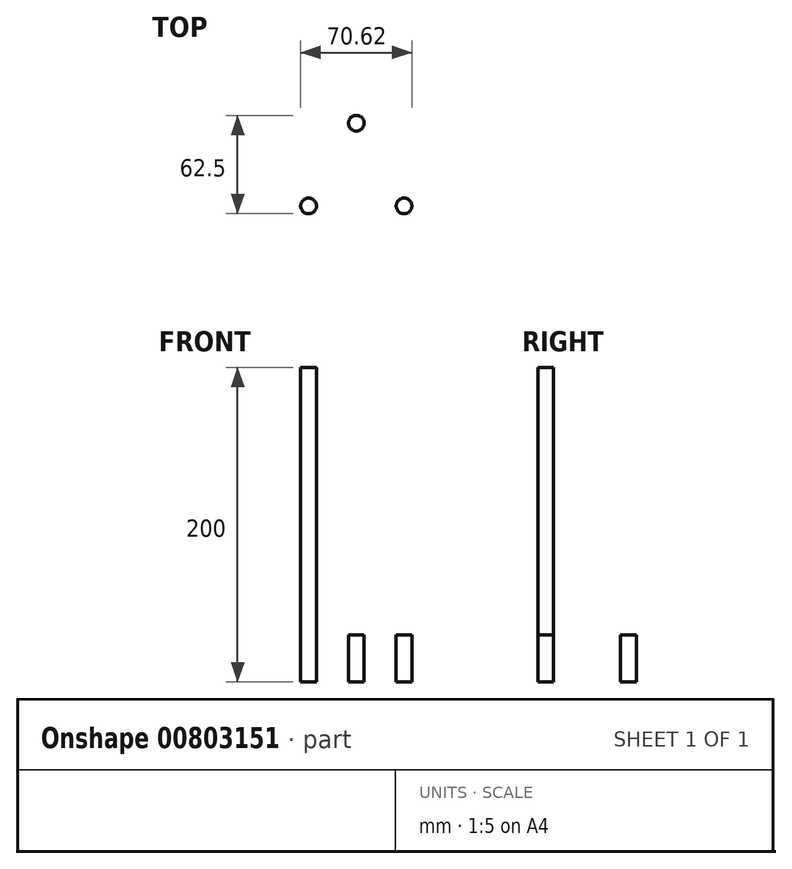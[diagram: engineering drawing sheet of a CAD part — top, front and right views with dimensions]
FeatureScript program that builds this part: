
annotation { "Feature Type Name" : "Feature", "Feature Type Description" : "" }
export const myFeature = defineFeature(function(context is Context, id is Id, definition is map)
    precondition{}
    {
        {
            var Q0;
            Q0=qCreatedBy(makeId("Front.planeOp"),FACE);
            var sketch = newSketch(context, id + "F0", { "sketchPlane" : qUnion([Q0])});
            skLineSegment(sketch, "E0", {"start": v(-35, 0) * mm, "end": v(35, 0) * mm});
            skPoint(sketch, "E1", {"position": v(0, 0) * mm});
            skLineSegment(sketch, "E2", {"start": v(10, 0) * mm, "end": v(-10, 0) * mm, "construction": true});
            skLineSegment(sketch, "E3", {"start": v(-10, 0) * mm, "end": v(10, 56.57) * mm});
            skLineSegment(sketch, "E4", {"start": v(10, 0) * mm, "end": v(-10, 56.57) * mm});
            skPoint(sketch, "E5.endSnap0", {"position": v(0, 28.28) * mm});
            skLineSegment(sketch, "E6", {"start": v(-10, 56.57) * mm, "end": v(10, 113.14) * mm});
            skLineSegment(sketch, "E7", {"start": v(10, 56.57) * mm, "end": v(-10, 113.14) * mm});
            skPoint(sketch, "E8", {"position": v(0, 84.85) * mm});
            skLineSegment(sketch, "E9", {"start": v(-10, 113.14) * mm, "end": v(0, 141.42) * mm});
            skLineSegment(sketch, "E10", {"start": v(0, 141.42) * mm, "end": v(10, 113.14) * mm});
            skLineSegment(sketch, "E11", {"start": v(0, 141.42) * mm, "end": v(-10, 169.7) * mm});
            skLineSegment(sketch, "E12", {"start": v(0, 141.42) * mm, "end": v(10, 169.7) * mm});
            skLineSegment(sketch, "E13", {"start": v(10, 169.7) * mm, "end": v(0, 197.99) * mm});
            skLineSegment(sketch, "E14", {"start": v(0, 197.99) * mm, "end": v(-10, 169.7) * mm});
            skSolve(sketch);
        }
        {
            var Q0;
            Q0=qCreatedBy(makeId("Top.planeOp"),FACE);
            var sketch = newSketch(context, id + "F1", { "sketchPlane" : qUnion([Q0])});
            skCircle(sketch, "E15", {"center": v(0, 35) * mm, "radius": 5 * mm});
            skCircle(sketch, "E16.1.0", {"center": v(-30.31, -17.5) * mm, "radius": 5 * mm});
            skCircle(sketch, "E16.2.0", {"center": v(30.31, -17.5) * mm, "radius": 5 * mm});
            skPoint(sketch, "E16.center", {"position": v(0, 0) * mm});
            skSolve(sketch);
        }
        {
            var Q0;
            Q0=makeQuery(id+"F1.imprint","IMPRINT",FACE,{"disambiguationData":[TD([[makeQuery(id+"F1.imprint","IMPRINT",EDGE,{"derivedFrom":sQuery(id+"F1.wireOp",EDGE,"E15")}),1.0]])]});
            extrude(context, id + "F2", {"entities" : qUnion([Q0]), "depth" : 30 * mm, "offsetDistance" : 25 * mm});
        }
        {
            var Q0;
            Q0=makeQuery(id+"F1.imprint","IMPRINT",FACE,{"disambiguationData":[TD([[makeQuery(id+"F1.imprint","IMPRINT",EDGE,{"derivedFrom":sQuery(id+"F1.wireOp",EDGE,"E16.1.0")}),1.0]])]});
            extrude(context, id + "F3", {"entities" : qUnion([Q0]), "depth" : 200 * mm, "offsetDistance" : 25 * mm});
        }
        {
            var Q0;
            Q0=makeQuery(id+"F1.imprint","IMPRINT",FACE,{"disambiguationData":[TD([[makeQuery(id+"F1.imprint","IMPRINT",EDGE,{"derivedFrom":sQuery(id+"F1.wireOp",EDGE,"E16.2.0")}),1.0]])]});
            var Q1;
            Q1=sQuery(id+"F1.wireOp",EDGE,"E16.2.0");
            extrude(context, id + "F4", {"entities" : qUnion([Q0]), "surfaceEntities" : qUnion([Q1]), "depth" : 30 * mm, "offsetDistance" : 25 * mm});
        }
    });
